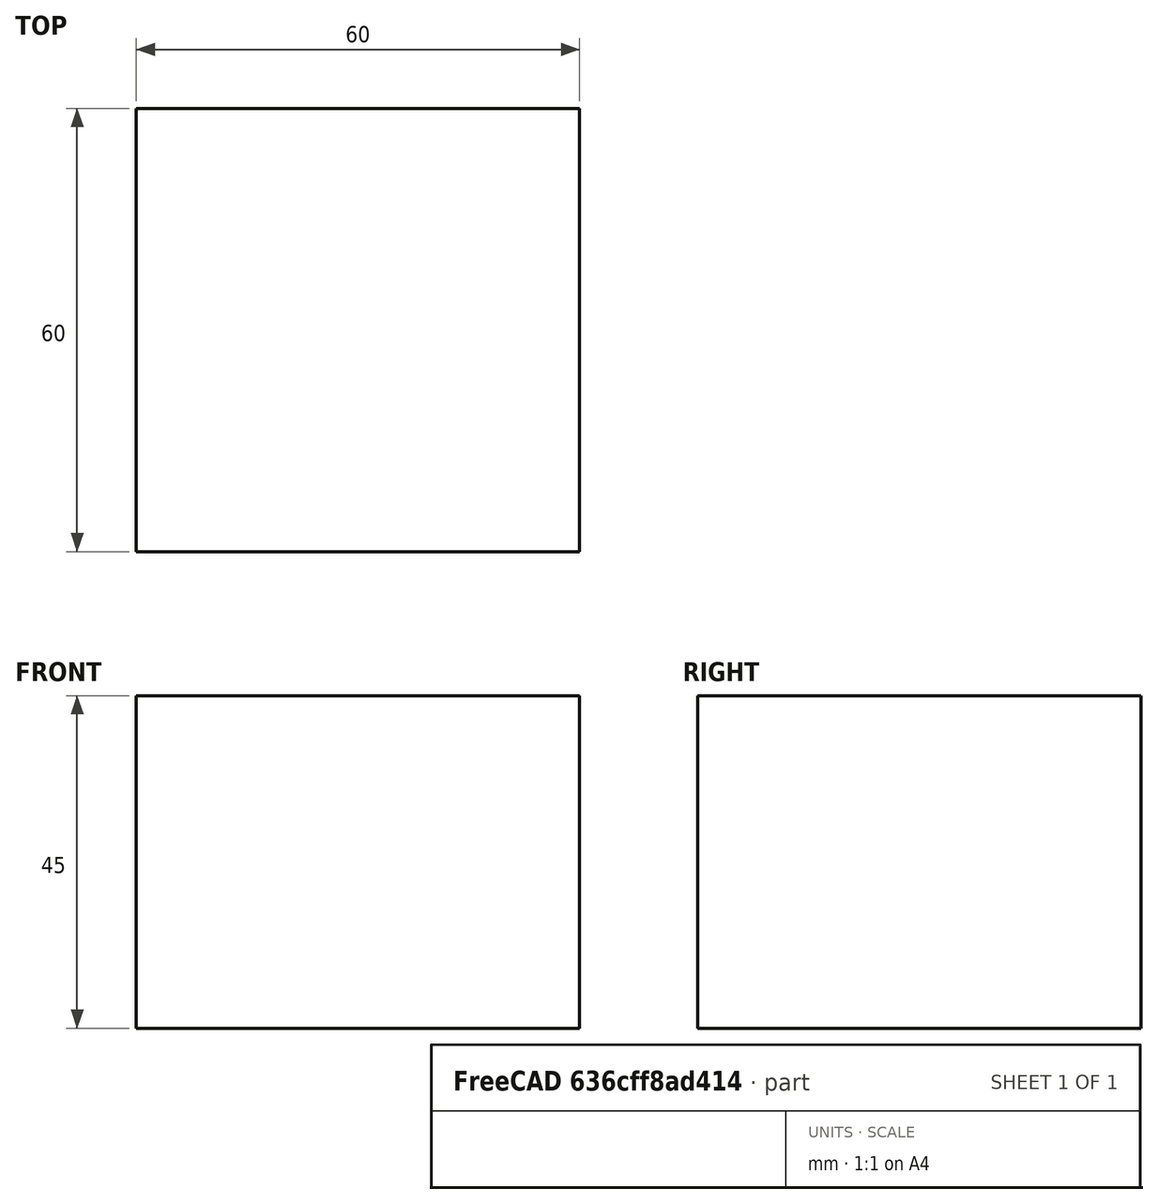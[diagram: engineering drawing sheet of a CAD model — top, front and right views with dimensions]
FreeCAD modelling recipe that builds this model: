
FCSTD DOCUMENT  (FreeCAD 0.18R16110 (Git))
Label: cad
License: All rights reserved
LicenseURL: http://en.wikipedia.org/wiki/All_rights_reserved
objects: Part::Box×1, Sketcher::SketchObject×1
note: 2 computed .brp shape members not serialized (recipe doc carries the construction recipe); baked Part::Feature solids carry a one-line shape summary decoded from their .brp

FEATURE [Part::Box] Box  label="Cubo"
  AttacherType = Attacher::AttachEngine3D
  Height = 45
  Length = 60
  Width = 60
FEATURE [Sketcher::SketchObject] Sketch
  MapMode = 5
  Placement = pos=(0,0,45) rot=(0,0,1;0rad)
  Support = -> [Box]
  sketch-geometry (20):
    g0: LineSegment StartX=10.0743 StartY=49.8281 StartZ=0 EndX=50.4218 EndY=49.8281 EndZ=0
    g1: LineSegment StartX=50.4218 StartY=49.8281 StartZ=0 EndX=50.2604 EndY=39.8219 EndZ=0
    g2: LineSegment StartX=50.2604 StartY=39.8219 StartZ=0 EndX=45.2573 EndY=39.6605 EndZ=0
    g3: LineSegment StartX=45.2573 StartY=39.6605 StartZ=0 EndX=45.4187 EndY=33.0435 EndZ=0
    g4: LineSegment StartX=45.4187 StartY=33.0435 StartZ=0 EndX=50.099 EndY=33.2049 EndZ=0
    g5: LineSegment StartX=50.099 StartY=33.2049 StartZ=0 EndX=50.2604 EndY=26.5879 EndZ=0
    g6: LineSegment StartX=50.2604 StartY=26.5879 StartZ=0 EndX=45.2573 EndY=26.2651 EndZ=0
    g7: LineSegment StartX=45.2573 StartY=26.2651 StartZ=0 EndX=45.0959 EndY=19.6481 EndZ=0
    g8: LineSegment StartX=45.0959 StartY=19.6481 StartZ=0 EndX=50.099 EndY=19.8095 EndZ=0
    g9: LineSegment StartX=50.099 StartY=19.8095 StartZ=0 EndX=49.9377 EndY=9.80332 EndZ=0
    g10: LineSegment StartX=49.9377 StartY=9.80332 StartZ=0 EndX=9.9129 EndY=9.96471 EndZ=0
    g11: LineSegment StartX=9.9129 StartY=9.96471 StartZ=0 EndX=9.7515 EndY=19.9709 EndZ=0
    g12: LineSegment StartX=9.7515 StartY=19.9709 StartZ=0 EndX=14.7546 EndY=19.9709 EndZ=0
    g13: LineSegment StartX=14.7546 StartY=19.9709 StartZ=0 EndX=14.5932 EndY=26.5879 EndZ=0
    g14: LineSegment StartX=14.5932 StartY=26.5879 StartZ=0 EndX=9.59012 EndY=26.7493 EndZ=0
    g15: LineSegment StartX=9.59012 StartY=26.7493 StartZ=0 EndX=9.7515 EndY=33.3663 EndZ=0
    g16: LineSegment StartX=9.7515 StartY=33.3663 StartZ=0 EndX=14.7546 EndY=33.3663 EndZ=0
    g17: LineSegment StartX=14.7546 StartY=33.3663 StartZ=0 EndX=14.5932 EndY=39.9833 EndZ=0
    g18: LineSegment StartX=14.5932 StartY=39.9833 StartZ=0 EndX=9.7515 EndY=39.8219 EndZ=0
    g19: LineSegment StartX=9.7515 StartY=39.8219 StartZ=0 EndX=9.7515 EndY=49.8281 EndZ=0
  constraints (17):
    c: Coincident(g0,g1)
    c: Coincident(g1,g2)
    c: Coincident(g2,g3)
    c: Coincident(g3,g4)
    c: Coincident(g4,g5)
    c: Coincident(g6,g7)
    c: Coincident(g7,g8)
    c: Coincident(g9,g10)
    c: Coincident(g10,g11)
    c: Coincident(g11,g12)
    c: Coincident(g12,g13)
    c: Coincident(g13,g14)
    c: Coincident(g14,g15)
    c: Coincident(g15,g16)
    c: Coincident(g16,g17)
    c: Coincident(g17,g18)
    c: Coincident(g18,g19)
